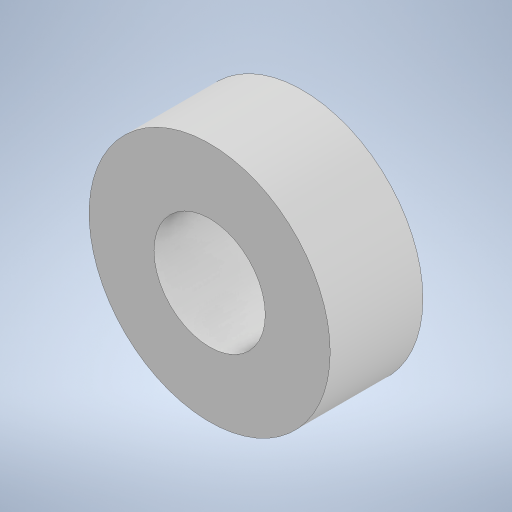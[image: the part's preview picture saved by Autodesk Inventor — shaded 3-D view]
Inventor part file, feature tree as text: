
AUTODESK INVENTOR PART (.ipt)
format: ipt  version: 2023 (Build 270158000, 158)  size: 291,840 bytes
history: native  units: in
note: dims shown in document units (in); Inventor stores cm internally (conversion verified against a paired STEP export)
features: extrude x2, sketch x2
ambient origin geometry x8: Origin, YZ Plane, XZ Plane, XY Plane, X Axis, Y Axis, Z Axis, Center Point
bodies: Solid1 (feature_tree)
feature tree (4):
  extrude  "Extrusion1"  Depth=4.7244in
  extrude  "Extrusion2"  Depth=0.1969in
  sketch  "Sketch1"  dims[d0=0.5118in d5=4.7244in]
  sketch  "Sketch2"  dims[d6=0.1969in d7=0.0in d8=4.7244in d9=0.2362in d10=8.2677in d12=360.0deg d14=0.0in d15=0.0in]
